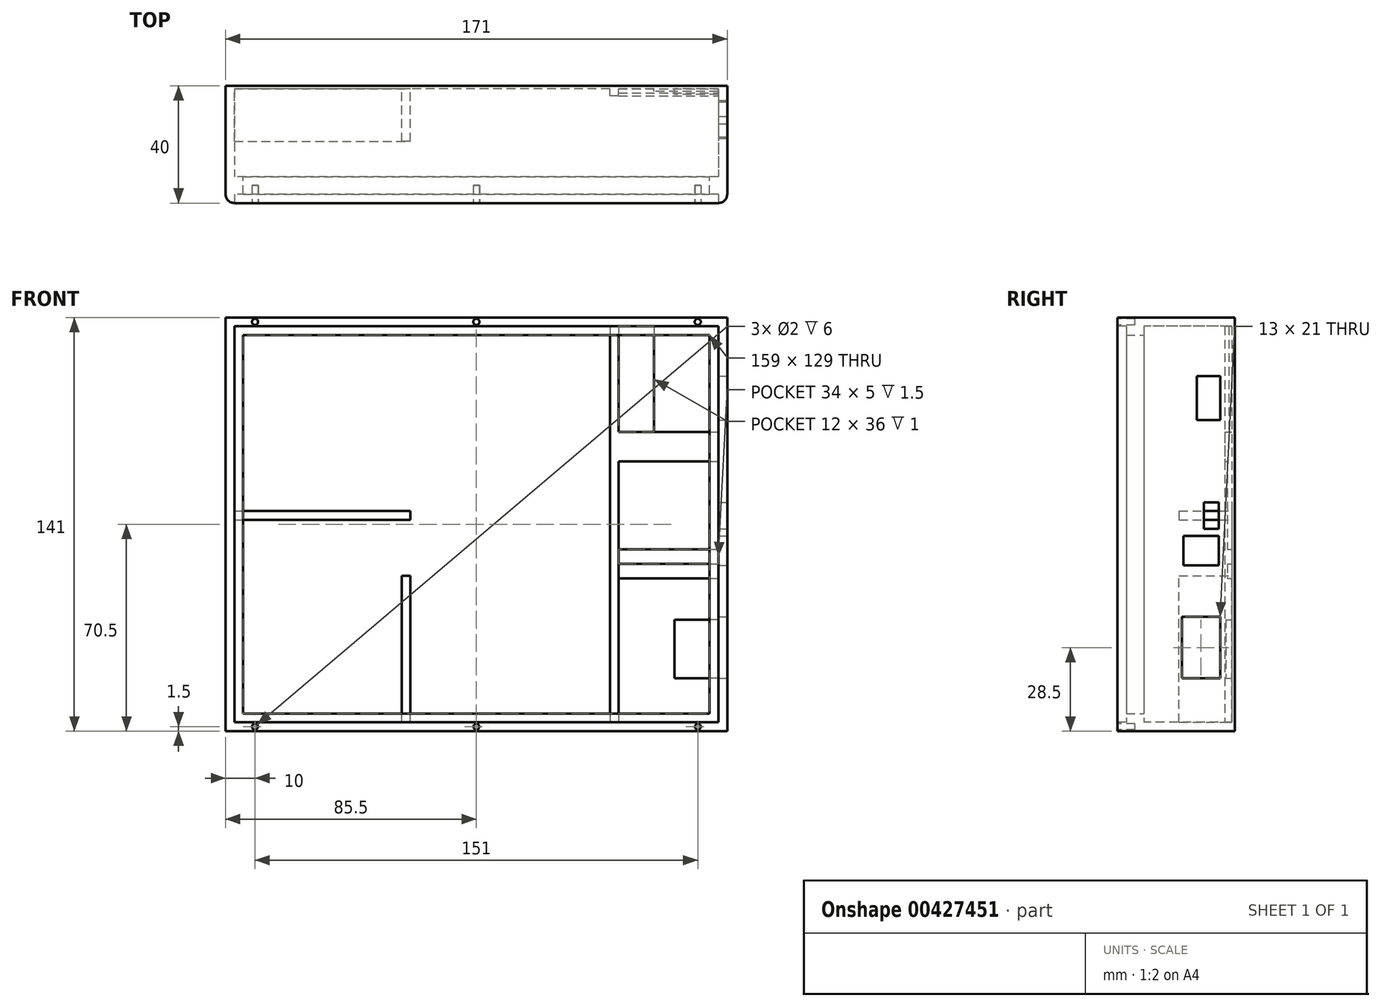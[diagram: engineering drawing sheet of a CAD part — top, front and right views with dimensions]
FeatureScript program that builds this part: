
annotation { "Feature Type Name" : "Feature", "Feature Type Description" : "" }
export const myFeature = defineFeature(function(context is Context, id is Id, definition is map)
    precondition{}
    {
        {
            var Q0;
            Q0=qCreatedBy(makeId("Front.planeOp"),FACE);
            var sketch = newSketch(context, id + "F0", { "sketchPlane" : qUnion([Q0])});
            skLineSegment(sketch, "E0.bottom", {"start": v(0, 0) * mm, "end": v(171, 0) * mm});
            skLineSegment(sketch, "E0.top", {"start": v(0, 141) * mm, "end": v(171, 141) * mm});
            skLineSegment(sketch, "E0.left", {"start": v(0, 0) * mm, "end": v(0, 141) * mm});
            skLineSegment(sketch, "E0.right", {"start": v(171, 0) * mm, "end": v(171, 141) * mm});
            skSolve(sketch);
        }
        {
            var Q0;
            Q0 = qSketchRegion(id + "F0", true);
            extrude(context, id + "F1", {"entities" : qUnion([Q0]), "depth" : 40 * mm});
        }
        {
            var Q0;
            Q0=makeQuery(id+"F1.opExtrude","CAP_FACE",FACE,{"disambiguationData":[OSD([sQuery(id+"F0.wireOp",EDGE,"E0.bottom"),sQuery(id+"F0.wireOp",EDGE,"E0.top"),sQuery(id+"F0.wireOp",EDGE,"E0.left"),sQuery(id+"F0.wireOp",EDGE,"E0.right")])],"isStart":false});
            var sketch = newSketch(context, id + "F2", { "sketchPlane" : qUnion([Q0])});
            skLineSegment(sketch, "E1", {"start": v(85.5, 141) * mm, "end": v(85.5, 0) * mm});
            skLineSegment(sketch, "E2", {"start": v(0, 70.5) * mm, "end": v(171, 70.5) * mm});
            skLineSegment(sketch, "E3.bottom", {"start": v(168, 138) * mm, "end": v(3, 138) * mm});
            skLineSegment(sketch, "E3.top", {"start": v(168, 3) * mm, "end": v(3, 3) * mm});
            skLineSegment(sketch, "E3.left", {"start": v(168, 138) * mm, "end": v(168, 3) * mm});
            skLineSegment(sketch, "E3.right", {"start": v(3, 138) * mm, "end": v(3, 3) * mm});
            skPoint(sketch, "E3.middle", {"position": v(85.5, 70.5) * mm});
            skSolve(sketch);
        }
        {
            var Q0;
            Q0 = qSketchRegion(id + "F2", true);
            extrude(context, id + "F3", {"entities" : qUnion([Q0]), "operationType" : NewBodyOperationType.REMOVE, "oppositeDirection" : true, "depth" : 3 * mm});
        }
        {
            var Q0;
            Q0=makeQuery(id+"F3.boolean.opBoolean","COPY",FACE,{"derivedFrom":makeQuery(id+"F3.opExtrude","CAP_FACE",FACE,{"disambiguationData":[OSD([sQuery(id+"F2.wireOp",EDGE,"E3.bottom"),sQuery(id+"F2.wireOp",EDGE,"E3.top"),sQuery(id+"F2.wireOp",EDGE,"E3.left"),sQuery(id+"F2.wireOp",EDGE,"E3.right")])],"isStart":false})});
            var sketch = newSketch(context, id + "F4", { "sketchPlane" : qUnion([Q0])});
            skLineSegment(sketch, "E4.bottom", {"start": v(3, 138) * mm, "end": v(168, 138) * mm});
            skLineSegment(sketch, "E4.top", {"start": v(3, 3) * mm, "end": v(168, 3) * mm});
            skLineSegment(sketch, "E4.left", {"start": v(3, 138) * mm, "end": v(3, 3) * mm});
            skLineSegment(sketch, "E4.right", {"start": v(168, 138) * mm, "end": v(168, 3) * mm});
            skLineSegment(sketch, "E5", {"start": v(85.5, 138) * mm, "end": v(85.5, 3) * mm});
            skLineSegment(sketch, "E6", {"start": v(3, 70.5) * mm, "end": v(168, 70.5) * mm});
            skLineSegment(sketch, "E7.bottom", {"start": v(166, 136) * mm, "end": v(5, 136) * mm});
            skLineSegment(sketch, "E7.top", {"start": v(166, 5) * mm, "end": v(5, 5) * mm});
            skLineSegment(sketch, "E7.left", {"start": v(166, 136) * mm, "end": v(166, 5) * mm});
            skLineSegment(sketch, "E7.right", {"start": v(5, 136) * mm, "end": v(5, 5) * mm});
            skPoint(sketch, "E7.middle", {"position": v(85.5, 70.5) * mm});
            skSolve(sketch);
        }
        {
            var Q0;
            {var subQ0=sQuery(id+"F4.wireOp",EDGE,"E7.bottom");var subQ1=sQuery(id+"F4.wireOp",EDGE,"E5");var subQ2=makeQuery(id+"F4.imprint","INTERSECT",VERTEX,{"derivedFrom":[subQ1,subQ0]});Q0=makeQuery(id+"F4.imprint","IMPRINT",FACE,{"disambiguationData":[TD([[makeQuery(id+"F4.imprint","IMPRINT",EDGE,{"disambiguationData":[TD([[subQ2,-1.0]])],"derivedFrom":subQ1}),-1.0]])]});}
            var Q1;
            {var subQ0=sQuery(id+"F4.wireOp",EDGE,"E7.bottom");var subQ1=sQuery(id+"F4.wireOp",EDGE,"E5");var subQ2=makeQuery(id+"F4.imprint","INTERSECT",VERTEX,{"derivedFrom":[subQ1,subQ0]});Q1=makeQuery(id+"F4.imprint","IMPRINT",FACE,{"disambiguationData":[TD([[makeQuery(id+"F4.imprint","IMPRINT",EDGE,{"disambiguationData":[TD([[subQ2,-1.0]])],"derivedFrom":subQ1}),1.0]])]});}
            var Q2;
            {var subQ0=sQuery(id+"F4.wireOp",EDGE,"E6");var subQ1=sQuery(id+"F4.wireOp",EDGE,"E5");var subQ2=makeQuery(id+"F4.imprint","INTERSECT",VERTEX,{"derivedFrom":[subQ1,subQ0]});Q2=makeQuery(id+"F4.imprint","IMPRINT",FACE,{"disambiguationData":[TD([[makeQuery(id+"F4.imprint","IMPRINT",EDGE,{"disambiguationData":[TD([[subQ2,-1.0]])],"derivedFrom":subQ1}),1.0]])]});}
            var Q3;
            {var subQ0=sQuery(id+"F4.wireOp",EDGE,"E6");var subQ1=sQuery(id+"F4.wireOp",EDGE,"E5");var subQ2=makeQuery(id+"F4.imprint","INTERSECT",VERTEX,{"derivedFrom":[subQ1,subQ0]});Q3=makeQuery(id+"F4.imprint","IMPRINT",FACE,{"disambiguationData":[TD([[makeQuery(id+"F4.imprint","IMPRINT",EDGE,{"disambiguationData":[TD([[subQ2,-1.0]])],"derivedFrom":subQ1}),-1.0]])]});}
            extrude(context, id + "F5", {"entities" : qUnion([Q0, Q1, Q2, Q3]), "operationType" : NewBodyOperationType.REMOVE, "oppositeDirection" : true, "depth" : 3 * mm});
        }
        {
            var Q0;
            Q0=makeQuery(id+"F3.boolean.opBoolean","COPY",FACE,{"derivedFrom":makeQuery(id+"F3.opExtrude","CAP_FACE",FACE,{"disambiguationData":[OSD([sQuery(id+"F2.wireOp",EDGE,"E3.bottom"),sQuery(id+"F2.wireOp",EDGE,"E3.top"),sQuery(id+"F2.wireOp",EDGE,"E3.left"),sQuery(id+"F2.wireOp",EDGE,"E3.right")])],"isStart":false})});
            var sketch = newSketch(context, id + "F6", { "sketchPlane" : qUnion([Q0])});
            skLineSegment(sketch, "E8", {"start": v(85.5, 138) * mm, "end": v(85.5, 3) * mm});
            skLineSegment(sketch, "E9", {"start": v(3, 70.5) * mm, "end": v(168, 70.5) * mm});
            skLineSegment(sketch, "E10.bottom", {"start": v(3, 138) * mm, "end": v(85.5, 138) * mm});
            skLineSegment(sketch, "E10.top", {"start": v(3, 70.5) * mm, "end": v(85.5, 70.5) * mm});
            skLineSegment(sketch, "E10.left", {"start": v(3, 138) * mm, "end": v(3, 70.5) * mm});
            skLineSegment(sketch, "E10.right", {"start": v(85.5, 138) * mm, "end": v(85.5, 70.5) * mm});
            skLineSegment(sketch, "E11.bottom", {"start": v(168, 138) * mm, "end": v(85.5, 138) * mm});
            skLineSegment(sketch, "E11.top", {"start": v(168, 70.5) * mm, "end": v(85.5, 70.5) * mm});
            skLineSegment(sketch, "E11.left", {"start": v(168, 138) * mm, "end": v(168, 70.5) * mm});
            skLineSegment(sketch, "E12.bottom", {"start": v(168, 3) * mm, "end": v(85.5, 3) * mm});
            skLineSegment(sketch, "E12.left", {"start": v(168, 3) * mm, "end": v(168, 70.5) * mm});
            skLineSegment(sketch, "E12.right", {"start": v(85.5, 3) * mm, "end": v(85.5, 70.5) * mm});
            skLineSegment(sketch, "E13.bottom", {"start": v(3, 3) * mm, "end": v(85.5, 3) * mm});
            skLineSegment(sketch, "E13.left", {"start": v(3, 3) * mm, "end": v(3, 70.5) * mm});
            skSolve(sketch);
        }
        {
            var Q0;
            Q0 = qSketchRegion(id + "F6", true);
            extrude(context, id + "F7", {"entities" : qUnion([Q0]), "operationType" : NewBodyOperationType.REMOVE, "oppositeDirection" : true, "depth" : 36 * mm});
        }
        {
            var Q0;
            Q0=makeQuery(id+"F7.boolean.opBoolean","COPY",FACE,{"derivedFrom":makeQuery(id+"F7.opExtrude","CAP_FACE",FACE,{"disambiguationData":[OSD([sQuery(id+"F6.wireOp",EDGE,"E10.bottom"),sQuery(id+"F6.wireOp",EDGE,"E10.left"),sQuery(id+"F6.wireOp",EDGE,"E11.bottom"),sQuery(id+"F6.wireOp",EDGE,"E11.left"),sQuery(id+"F6.wireOp",EDGE,"E12.bottom"),sQuery(id+"F6.wireOp",EDGE,"E12.left"),sQuery(id+"F6.wireOp",EDGE,"E13.bottom"),sQuery(id+"F6.wireOp",EDGE,"E13.left")])],"isStart":false})});
            var sketch = newSketch(context, id + "F8", { "sketchPlane" : qUnion([Q0])});
            skLineSegment(sketch, "E14.bottom", {"start": v(3, 3) * mm, "end": v(168, 3) * mm});
            skLineSegment(sketch, "E14.top", {"start": v(3, 138) * mm, "end": v(168, 138) * mm});
            skLineSegment(sketch, "E14.left", {"start": v(3, 3) * mm, "end": v(3, 138) * mm});
            skLineSegment(sketch, "E14.right", {"start": v(168, 3) * mm, "end": v(168, 138) * mm});
            skLineSegment(sketch, "E15", {"start": v(85.5, 3) * mm, "end": v(85.5, 138) * mm});
            skLineSegment(sketch, "E16", {"start": v(3, 70.5) * mm, "end": v(168, 70.5) * mm});
            skLineSegment(sketch, "E17.bottom", {"start": v(6, 135) * mm, "end": v(165, 135) * mm});
            skLineSegment(sketch, "E17.top", {"start": v(6, 6) * mm, "end": v(165, 6) * mm});
            skLineSegment(sketch, "E17.left", {"start": v(6, 135) * mm, "end": v(6, 6) * mm});
            skLineSegment(sketch, "E17.right", {"start": v(165, 135) * mm, "end": v(165, 6) * mm});
            skPoint(sketch, "E17.middle", {"position": v(85.5, 70.5) * mm});
            skSolve(sketch);
        }
        {
            var Q0;
            {var subQ1=sQuery(id+"F8.wireOp",EDGE,"E14.left");var subQ6=sQuery(id+"F8.wireOp",EDGE,"E14.top");var subQ10=makeQuery(id+"F8.imprint","INTERSECT",VERTEX,{"derivedFrom":[subQ6,subQ1]});Q0=makeQuery(id+"F8.imprint","IMPRINT",FACE,{"disambiguationData":[TD([[makeQuery(id+"F8.imprint","IMPRINT",EDGE,{"disambiguationData":[TD([[subQ10,1.0]])],"derivedFrom":subQ6}),1.0]])]});}
            var Q1;
            {var subQ1=sQuery(id+"F8.wireOp",EDGE,"E14.left");var subQ5=sQuery(id+"F8.wireOp",EDGE,"E14.bottom");var subQ6=makeQuery(id+"F8.imprint","INTERSECT",VERTEX,{"derivedFrom":[subQ5,subQ1]});Q1=makeQuery(id+"F8.imprint","IMPRINT",FACE,{"disambiguationData":[TD([[makeQuery(id+"F8.imprint","IMPRINT",EDGE,{"disambiguationData":[TD([[subQ6,1.0]])],"derivedFrom":subQ5}),-1.0]])]});}
            var Q2;
            {var subQ1=sQuery(id+"F8.wireOp",EDGE,"E14.bottom");var subQ7=sQuery(id+"F8.wireOp",EDGE,"E14.right");var subQ8=makeQuery(id+"F8.imprint","INTERSECT",VERTEX,{"derivedFrom":[subQ1,subQ7]});Q2=makeQuery(id+"F8.imprint","IMPRINT",FACE,{"disambiguationData":[TD([[makeQuery(id+"F8.imprint","IMPRINT",EDGE,{"disambiguationData":[TD([[subQ8,-1.0]])],"derivedFrom":subQ1}),-1.0]])]});}
            var Q3;
            {var subQ1=sQuery(id+"F8.wireOp",EDGE,"E14.right");var subQ6=sQuery(id+"F8.wireOp",EDGE,"E14.top");var subQ11=makeQuery(id+"F8.imprint","INTERSECT",VERTEX,{"derivedFrom":[subQ6,subQ1]});Q3=makeQuery(id+"F8.imprint","IMPRINT",FACE,{"disambiguationData":[TD([[makeQuery(id+"F8.imprint","IMPRINT",EDGE,{"disambiguationData":[TD([[subQ11,-1.0]])],"derivedFrom":subQ6}),1.0]])]});}
            extrude(context, id + "F9", {"entities" : qUnion([Q0, Q1, Q2, Q3]), "operationType" : NewBodyOperationType.ADD, "depth" : 36 * mm, "hasSecondDirection" : true, "secondDirectionOppositeDirection" : false, "secondDirectionDepth" : 30 * mm});
        }
        {
            var Q0;
            Q0=makeQuery(id+"F1.opExtrude","SWEPT_FACE",FACE,{"disambiguationData":[OSD([sQuery(id+"F0.wireOp",EDGE,"E0.right")])]});
            var sketch = newSketch(context, id + "F10", { "sketchPlane" : qUnion([Q0])});
            skLineSegment(sketch, "E18.bottom", {"start": v(-13, 106) * mm, "end": v(-5, 106) * mm});
            skLineSegment(sketch, "E18.top", {"start": v(-13, 121) * mm, "end": v(-5, 121) * mm});
            skLineSegment(sketch, "E18.left", {"start": v(-13, 106) * mm, "end": v(-13, 121) * mm});
            skLineSegment(sketch, "E18.right", {"start": v(-5, 106) * mm, "end": v(-5, 121) * mm});
            skLineSegment(sketch, "E19", {"start": v(-9, 121) * mm, "end": v(-9, 141) * mm});
            skLineSegment(sketch, "E20", {"start": v(-5, 113.5) * mm, "end": v(0, 113.5) * mm});
            skSolve(sketch);
        }
        {
            var Q0;
            {var subQ5=sQuery(id+"F10.wireOp",EDGE,"E18.bottom");Q0=makeQuery(id+"F10.imprint","IMPRINT",FACE,{"disambiguationData":[TD([[makeQuery(id+"F10.imprint","IMPRINT",EDGE,{"derivedFrom":subQ5}),1.0]])]});}
            extrude(context, id + "F11", {"entities" : qUnion([Q0]), "operationType" : NewBodyOperationType.REMOVE, "oppositeDirection" : true, "depth" : 39.9 * mm});
        }
        {
            var Q0;
            Q0=makeQuery(id+"F1.opExtrude","CAP_EDGE",EDGE,{"disambiguationData":[OSD([sQuery(id+"F0.wireOp",EDGE,"E0.right")])],"isStart":false});
            fillet(context, id + "F12", {"entities" : qUnion([Q0]), "radius" : 3 * mm, "tangentPropagation" : true, "allowEdgeOverflow" : false});
        }
        {
            var Q0;
            Q0=makeQuery(id+"F1.opExtrude","CAP_EDGE",EDGE,{"disambiguationData":[OSD([sQuery(id+"F0.wireOp",EDGE,"E0.left")])],"isStart":false});
            fillet(context, id + "F13", {"entities" : qUnion([Q0]), "radius" : 3 * mm, "tangentPropagation" : true, "allowEdgeOverflow" : false});
        }
        {
            var Q0;
            Q0=makeQuery(id+"F1.opExtrude","SWEPT_FACE",FACE,{"disambiguationData":[OSD([sQuery(id+"F0.wireOp",EDGE,"E0.right")])]});
            var sketch = newSketch(context, id + "F14", { "sketchPlane" : qUnion([Q0])});
            skLineSegment(sketch, "E21.bottom", {"start": v(-10.5, 69) * mm, "end": v(-5.5, 69) * mm});
            skLineSegment(sketch, "E21.top", {"start": v(-10.5, 78) * mm, "end": v(-5.5, 78) * mm});
            skLineSegment(sketch, "E21.left", {"start": v(-10.5, 69) * mm, "end": v(-10.5, 78) * mm});
            skLineSegment(sketch, "E21.right", {"start": v(-5.5, 69) * mm, "end": v(-5.5, 78) * mm});
            skLineSegment(sketch, "E22", {"start": v(-8, 78) * mm, "end": v(-8, 138) * mm});
            skLineSegment(sketch, "E23", {"start": v(-5.5, 73.5) * mm, "end": v(0, 73.5) * mm});
            skSolve(sketch);
        }
        {
            var Q0;
            {var subQ5=sQuery(id+"F14.wireOp",EDGE,"E21.bottom");Q0=makeQuery(id+"F14.imprint","IMPRINT",FACE,{"disambiguationData":[TD([[makeQuery(id+"F14.imprint","IMPRINT",EDGE,{"derivedFrom":subQ5}),1.0]])]});}
            extrude(context, id + "F15", {"entities" : qUnion([Q0]), "operationType" : NewBodyOperationType.REMOVE, "oppositeDirection" : true, "depth" : 87.6 * mm});
        }
        {
            var Q0;
            Q0=makeQuery(id+"F1.opExtrude","SWEPT_FACE",FACE,{"disambiguationData":[OSD([sQuery(id+"F0.wireOp",EDGE,"E0.right")])]});
            var sketch = newSketch(context, id + "F16", { "sketchPlane" : qUnion([Q0])});
            skLineSegment(sketch, "E24.bottom", {"start": v(-17.5, 56.5) * mm, "end": v(-5.5, 56.5) * mm});
            skLineSegment(sketch, "E24.top", {"start": v(-17.5, 66.5) * mm, "end": v(-5.5, 66.5) * mm});
            skLineSegment(sketch, "E24.left", {"start": v(-17.5, 56.5) * mm, "end": v(-17.5, 66.5) * mm});
            skLineSegment(sketch, "E24.right", {"start": v(-5.5, 56.5) * mm, "end": v(-5.5, 66.5) * mm});
            skLineSegment(sketch, "E25", {"start": v(-11.5, 66.5) * mm, "end": v(-11.5, 138) * mm});
            skLineSegment(sketch, "E26", {"start": v(-5.5, 61.5) * mm, "end": v(0, 61.5) * mm});
            skSolve(sketch);
        }
        {
            var Q0;
            {var subQ5=sQuery(id+"F16.wireOp",EDGE,"E24.bottom");Q0=makeQuery(id+"F16.imprint","IMPRINT",FACE,{"disambiguationData":[TD([[makeQuery(id+"F16.imprint","IMPRINT",EDGE,{"derivedFrom":subQ5}),1.0]])]});}
            extrude(context, id + "F17", {"entities" : qUnion([Q0]), "operationType" : NewBodyOperationType.REMOVE, "oppositeDirection" : true, "depth" : 58 * mm});
        }
        {
            var Q0;
            Q0=makeQuery(id+"F7.boolean.opBoolean","COPY",FACE,{"derivedFrom":makeQuery(id+"F7.opExtrude","CAP_FACE",FACE,{"disambiguationData":[OSD([sQuery(id+"F6.wireOp",EDGE,"E10.bottom"),sQuery(id+"F6.wireOp",EDGE,"E10.left"),sQuery(id+"F6.wireOp",EDGE,"E11.bottom"),sQuery(id+"F6.wireOp",EDGE,"E11.left"),sQuery(id+"F6.wireOp",EDGE,"E12.bottom"),sQuery(id+"F6.wireOp",EDGE,"E12.left"),sQuery(id+"F6.wireOp",EDGE,"E13.bottom"),sQuery(id+"F6.wireOp",EDGE,"E13.left")])],"isStart":false})});
            var sketch = newSketch(context, id + "F18", { "sketchPlane" : qUnion([Q0])});
            skLineSegment(sketch, "E27.bottom", {"start": v(131, 138) * mm, "end": v(134, 138) * mm});
            skLineSegment(sketch, "E27.top", {"start": v(131, 3) * mm, "end": v(134, 3) * mm});
            skLineSegment(sketch, "E27.left", {"start": v(131, 138) * mm, "end": v(131, 3) * mm});
            skLineSegment(sketch, "E27.right", {"start": v(134, 138) * mm, "end": v(134, 3) * mm});
            skLineSegment(sketch, "E28", {"start": v(134, 70.5) * mm, "end": v(168, 70.5) * mm});
            skLineSegment(sketch, "E29.bottom", {"start": v(134, 102) * mm, "end": v(168, 102) * mm});
            skLineSegment(sketch, "E29.top", {"start": v(134, 92) * mm, "end": v(168, 92) * mm});
            skLineSegment(sketch, "E29.left", {"start": v(134, 102) * mm, "end": v(134, 92) * mm});
            skLineSegment(sketch, "E29.right", {"start": v(168, 102) * mm, "end": v(168, 92) * mm});
            skLineSegment(sketch, "E30", {"start": v(151, 102) * mm, "end": v(151, 138) * mm});
            skSolve(sketch);
        }
        {
            var Q0;
            {var subQ1=sQuery(id+"F18.wireOp",EDGE,"E27.bottom");Q0=makeQuery(id+"F18.imprint","IMPRINT",FACE,{"disambiguationData":[TD([[makeQuery(id+"F18.imprint","IMPRINT",EDGE,{"derivedFrom":subQ1}),1.0]])]});}
            var Q1;
            Q1=makeQuery(id+"F18.imprint","IMPRINT",FACE,{"disambiguationData":[TD([[makeQuery(id+"F18.imprint","IMPRINT",EDGE,{"derivedFrom":sQuery(id+"F18.wireOp",EDGE,"E29.top")}),1.0]])]});
            extrude(context, id + "F19", {"entities" : qUnion([Q0, Q1]), "operationType" : NewBodyOperationType.ADD, "depth" : 2.5 * mm});
        }
        {
            var Q0;
            {var subQ0=sQuery(id+"F6.wireOp",EDGE,"E12.left");var subQ1=sQuery(id+"F6.wireOp",EDGE,"E11.left");var subQ2=sQuery(id+"F6.wireOp",EDGE,"E13.bottom");var subQ3=sQuery(id+"F6.wireOp",EDGE,"E12.bottom");var subQ4=sQuery(id+"F18.wireOp",EDGE,"E29.top");Q0=makeQuery(id+"F19.boolean.opBoolean","SPLIT",FACE,{"disambiguationData":[TD([makeQuery(id+"F19.opExtrude","SWEPT_FACE",FACE,{"disambiguationData":[OSD([subQ4])]})])],"derivedFrom":makeQuery(id+"F7.boolean.opBoolean","COPY",FACE,{"derivedFrom":makeQuery(id+"F7.opExtrude","CAP_FACE",FACE,{"disambiguationData":[OSD([sQuery(id+"F6.wireOp",EDGE,"E10.bottom"),sQuery(id+"F6.wireOp",EDGE,"E10.left"),sQuery(id+"F6.wireOp",EDGE,"E11.bottom"),subQ1,subQ3,subQ0,subQ2,sQuery(id+"F6.wireOp",EDGE,"E13.left")])],"isStart":false})})});}
            var sketch = newSketch(context, id + "F20", { "sketchPlane" : qUnion([Q0])});
            skLineSegment(sketch, "E31.bottom", {"start": v(134, 92) * mm, "end": v(168, 92) * mm});
            skLineSegment(sketch, "E31.top", {"start": v(134, 62) * mm, "end": v(168, 62) * mm});
            skLineSegment(sketch, "E31.left", {"start": v(134, 92) * mm, "end": v(134, 62) * mm});
            skLineSegment(sketch, "E31.right", {"start": v(168, 92) * mm, "end": v(168, 62) * mm});
            skLineSegment(sketch, "E32.bottom", {"start": v(134, 57) * mm, "end": v(168, 57) * mm});
            skLineSegment(sketch, "E32.top", {"start": v(134, 52) * mm, "end": v(168, 52) * mm});
            skLineSegment(sketch, "E32.left", {"start": v(134, 57) * mm, "end": v(134, 52) * mm});
            skLineSegment(sketch, "E32.right", {"start": v(168, 57) * mm, "end": v(168, 52) * mm});
            skLineSegment(sketch, "E33", {"start": v(134, 62) * mm, "end": v(134, 57) * mm});
            skSolve(sketch);
        }
        {
            var Q0;
            Q0=makeQuery(id+"F20.imprint","IMPRINT",FACE,{"disambiguationData":[TD([[makeQuery(id+"F20.imprint","IMPRINT",EDGE,{"derivedFrom":sQuery(id+"F20.wireOp",EDGE,"E31.bottom")}),-1.0]])]});
            var Q1;
            Q1=makeQuery(id+"F20.imprint","IMPRINT",FACE,{"disambiguationData":[TD([[makeQuery(id+"F20.imprint","IMPRINT",EDGE,{"derivedFrom":sQuery(id+"F20.wireOp",EDGE,"E32.bottom")}),-1.0]])]});
            extrude(context, id + "F21", {"entities" : qUnion([Q0, Q1]), "operationType" : NewBodyOperationType.ADD, "depth" : 1.5 * mm});
        }
        {
            var Q0;
            {var subQ0=sQuery(id+"F6.wireOp",EDGE,"E12.left");var subQ1=sQuery(id+"F6.wireOp",EDGE,"E11.left");var subQ2=sQuery(id+"F18.wireOp",EDGE,"E29.bottom");var subQ3=sQuery(id+"F6.wireOp",EDGE,"E11.bottom");var subQ4=sQuery(id+"F6.wireOp",EDGE,"E10.bottom");Q0=makeQuery(id+"F19.boolean.opBoolean","SPLIT",FACE,{"disambiguationData":[TD([makeQuery(id+"F19.opExtrude","SWEPT_FACE",FACE,{"disambiguationData":[OSD([subQ2])]})])],"derivedFrom":makeQuery(id+"F7.boolean.opBoolean","COPY",FACE,{"derivedFrom":makeQuery(id+"F7.opExtrude","CAP_FACE",FACE,{"disambiguationData":[OSD([subQ4,sQuery(id+"F6.wireOp",EDGE,"E10.left"),subQ3,subQ1,sQuery(id+"F6.wireOp",EDGE,"E12.bottom"),subQ0,sQuery(id+"F6.wireOp",EDGE,"E13.bottom"),sQuery(id+"F6.wireOp",EDGE,"E13.left")])],"isStart":false})})});}
            var sketch = newSketch(context, id + "F22", { "sketchPlane" : qUnion([Q0])});
            skLineSegment(sketch, "E34.bottom", {"start": v(146, 138) * mm, "end": v(168, 138) * mm});
            skLineSegment(sketch, "E34.top", {"start": v(146, 102) * mm, "end": v(168, 102) * mm});
            skLineSegment(sketch, "E34.left", {"start": v(146, 138) * mm, "end": v(146, 102) * mm});
            skLineSegment(sketch, "E34.right", {"start": v(168, 138) * mm, "end": v(168, 102) * mm});
            skSolve(sketch);
        }
        {
            var Q0;
            Q0 = qSketchRegion(id + "F22", true);
            extrude(context, id + "F23", {"entities" : qUnion([Q0]), "operationType" : NewBodyOperationType.ADD, "depth" : 1 * mm});
        }
        {
            var Q0;
            Q0=makeQuery(id+"F1.opExtrude","SWEPT_FACE",FACE,{"disambiguationData":[OSD([sQuery(id+"F0.wireOp",EDGE,"E0.right")])]});
            var sketch = newSketch(context, id + "F24", { "sketchPlane" : qUnion([Q0])});
            skLineSegment(sketch, "E35.bottom", {"start": v(-18, 18) * mm, "end": v(-5, 18) * mm});
            skLineSegment(sketch, "E35.top", {"start": v(-18, 39) * mm, "end": v(-5, 39) * mm});
            skLineSegment(sketch, "E35.left", {"start": v(-18, 18) * mm, "end": v(-18, 39) * mm});
            skLineSegment(sketch, "E35.right", {"start": v(-5, 18) * mm, "end": v(-5, 39) * mm});
            skLineSegment(sketch, "E36", {"start": v(-11.5, 18) * mm, "end": v(-11.5, 3) * mm});
            skLineSegment(sketch, "E37", {"start": v(-5, 28.5) * mm, "end": v(0, 28.5) * mm});
            skSolve(sketch);
        }
        {
            var Q0;
            Q0 = qSketchRegion(id + "F24", true);
            extrude(context, id + "F25", {"entities" : qUnion([Q0]), "operationType" : NewBodyOperationType.REMOVE, "oppositeDirection" : true, "depth" : 107.7 * mm});
        }
        {
            var Q0;
            {var subQ0=sQuery(id+"F6.wireOp",EDGE,"E12.left");var subQ1=sQuery(id+"F6.wireOp",EDGE,"E11.left");var subQ4=sQuery(id+"F6.wireOp",EDGE,"E13.bottom");var subQ5=sQuery(id+"F6.wireOp",EDGE,"E12.bottom");var subQ7=makeQuery(id+"F3.boolean.opBoolean","COPY",FACE,{"derivedFrom":makeQuery(id+"F3.opExtrude","SWEPT_FACE",FACE,{"disambiguationData":[OSD([sQuery(id+"F2.wireOp",EDGE,"E3.top")])]})});var subQ10=sQuery(id+"F18.wireOp",EDGE,"E29.top");Q0=makeQuery(id+"F21.boolean.opBoolean","SPLIT",FACE,{"disambiguationData":[TD([subQ7])],"derivedFrom":makeQuery(id+"F19.boolean.opBoolean","SPLIT",FACE,{"disambiguationData":[TD([makeQuery(id+"F19.opExtrude","SWEPT_FACE",FACE,{"disambiguationData":[OSD([subQ10])]})])],"derivedFrom":makeQuery(id+"F7.boolean.opBoolean","COPY",FACE,{"derivedFrom":makeQuery(id+"F7.opExtrude","CAP_FACE",FACE,{"disambiguationData":[OSD([sQuery(id+"F6.wireOp",EDGE,"E10.bottom"),sQuery(id+"F6.wireOp",EDGE,"E10.left"),sQuery(id+"F6.wireOp",EDGE,"E11.bottom"),subQ1,subQ5,subQ0,subQ4,sQuery(id+"F6.wireOp",EDGE,"E13.left")])],"isStart":false})})})});}
            var sketch = newSketch(context, id + "F26", { "sketchPlane" : qUnion([Q0])});
            skLineSegment(sketch, "E38.bottom", {"start": v(168, 38) * mm, "end": v(153, 38) * mm});
            skLineSegment(sketch, "E38.top", {"start": v(168, 18) * mm, "end": v(153, 18) * mm});
            skLineSegment(sketch, "E38.left", {"start": v(168, 38) * mm, "end": v(168, 18) * mm});
            skLineSegment(sketch, "E38.right", {"start": v(153, 38) * mm, "end": v(153, 18) * mm});
            skLineSegment(sketch, "E39", {"start": v(160.5, 18) * mm, "end": v(160.5, 3) * mm});
            skSolve(sketch);
        }
        {
            var Q0;
            Q0 = qSketchRegion(id + "F26", true);
            extrude(context, id + "F27", {"entities" : qUnion([Q0]), "operationType" : NewBodyOperationType.ADD, "depth" : 2 * mm});
        }
        {
            var Q0;
            {var subQ0=sQuery(id+"F6.wireOp",EDGE,"E11.bottom");var subQ1=sQuery(id+"F6.wireOp",EDGE,"E10.bottom");var subQ2=sQuery(id+"F6.wireOp",EDGE,"E13.bottom");var subQ3=sQuery(id+"F6.wireOp",EDGE,"E12.bottom");var subQ4=sQuery(id+"F6.wireOp",EDGE,"E13.left");var subQ5=sQuery(id+"F6.wireOp",EDGE,"E10.left");Q0=makeQuery(id+"F19.boolean.opBoolean","SPLIT",FACE,{"disambiguationData":[TD([makeQuery(id+"F3.boolean.opBoolean","COPY",FACE,{"derivedFrom":makeQuery(id+"F3.opExtrude","SWEPT_FACE",FACE,{"disambiguationData":[OSD([sQuery(id+"F2.wireOp",EDGE,"E3.right")])]})})])],"derivedFrom":makeQuery(id+"F7.boolean.opBoolean","COPY",FACE,{"derivedFrom":makeQuery(id+"F7.opExtrude","CAP_FACE",FACE,{"disambiguationData":[OSD([subQ1,subQ5,subQ0,sQuery(id+"F6.wireOp",EDGE,"E11.left"),subQ3,sQuery(id+"F6.wireOp",EDGE,"E12.left"),subQ2,subQ4])],"isStart":false})})});}
            var sketch = newSketch(context, id + "F28", { "sketchPlane" : qUnion([Q0])});
            skLineSegment(sketch, "E40.bottom", {"start": v(3, 75) * mm, "end": v(63, 75) * mm});
            skLineSegment(sketch, "E40.top", {"start": v(3, 72) * mm, "end": v(63, 72) * mm});
            skLineSegment(sketch, "E40.left", {"start": v(3, 75) * mm, "end": v(3, 72) * mm});
            skLineSegment(sketch, "E40.right", {"start": v(63, 75) * mm, "end": v(63, 72) * mm});
            skLineSegment(sketch, "E41", {"start": v(33, 72) * mm, "end": v(33, 3) * mm});
            skLineSegment(sketch, "E42.bottom", {"start": v(63, 3) * mm, "end": v(60, 3) * mm});
            skLineSegment(sketch, "E42.top", {"start": v(63, 53) * mm, "end": v(60, 53) * mm});
            skLineSegment(sketch, "E42.left", {"start": v(63, 3) * mm, "end": v(63, 53) * mm});
            skLineSegment(sketch, "E42.right", {"start": v(60, 3) * mm, "end": v(60, 53) * mm});
            skLineSegment(sketch, "E43", {"start": v(60, 28) * mm, "end": v(3, 28) * mm});
            skSolve(sketch);
        }
        {
            var Q0;
            Q0 = qSketchRegion(id + "F28", true);
            extrude(context, id + "F29", {"entities" : qUnion([Q0]), "operationType" : NewBodyOperationType.ADD, "depth" : 18 * mm});
        }
        {
            var Q0;
            Q0=makeQuery(id+"F13.opFillet","SPLIT",FACE,{"disambiguationData":[OD(0.0)],"derivedFrom":makeQuery(id+"F1.opExtrude","CAP_FACE",FACE,{"disambiguationData":[OSD([sQuery(id+"F0.wireOp",EDGE,"E0.bottom"),sQuery(id+"F0.wireOp",EDGE,"E0.top"),sQuery(id+"F0.wireOp",EDGE,"E0.left"),sQuery(id+"F0.wireOp",EDGE,"E0.right")])],"isStart":false})});
            var sketch = newSketch(context, id + "F30", { "sketchPlane" : qUnion([Q0])});
            skCircle(sketch, "E44", {"center": v(10.05, 139.5) * mm, "radius": 1.05 * mm});
            skLineSegment(sketch, "E45", {"start": v(10.05, 139.5) * mm, "end": v(10.05, 141) * mm});
            skLineSegment(sketch, "E46", {"start": v(3, 139.5) * mm, "end": v(9, 139.5) * mm});
            skCircle(sketch, "E47", {"center": v(160.95, 139.5) * mm, "radius": 1.05 * mm});
            skLineSegment(sketch, "E48", {"start": v(160.95, 139.5) * mm, "end": v(160.95, 141) * mm});
            skLineSegment(sketch, "E49", {"start": v(168, 139.5) * mm, "end": v(162, 139.5) * mm});
            skLineSegment(sketch, "E50", {"start": v(3, 139.5) * mm, "end": v(168, 139.5) * mm});
            skCircle(sketch, "E51", {"center": v(85.5, 139.5) * mm, "radius": 1.05 * mm});
            skSolve(sketch);
        }
        {
            var Q0;
            Q0 = qSketchRegion(id + "F30", true);
            extrude(context, id + "F31", {"entities" : qUnion([Q0]), "operationType" : NewBodyOperationType.REMOVE, "oppositeDirection" : true, "depth" : 6 * mm});
        }
        {
            var Q0;
            Q0=makeQuery(id+"F13.opFillet","SPLIT",FACE,{"disambiguationData":[OD(1.0)],"derivedFrom":makeQuery(id+"F1.opExtrude","CAP_FACE",FACE,{"disambiguationData":[OSD([sQuery(id+"F0.wireOp",EDGE,"E0.bottom"),sQuery(id+"F0.wireOp",EDGE,"E0.top"),sQuery(id+"F0.wireOp",EDGE,"E0.left"),sQuery(id+"F0.wireOp",EDGE,"E0.right")])],"isStart":false})});
            var sketch = newSketch(context, id + "F32", { "sketchPlane" : qUnion([Q0])});
            skCircle(sketch, "E52", {"center": v(10, 1.5) * mm, "radius": 1 * mm});
            skLineSegment(sketch, "E53", {"start": v(10, 1.5) * mm, "end": v(10, 3) * mm});
            skLineSegment(sketch, "E54", {"start": v(3, 1.5) * mm, "end": v(9, 1.5) * mm});
            skCircle(sketch, "E55", {"center": v(161, 1.5) * mm, "radius": 1 * mm});
            skLineSegment(sketch, "E56", {"start": v(161, 1.5) * mm, "end": v(161, 3) * mm});
            skLineSegment(sketch, "E57", {"start": v(168, 1.5) * mm, "end": v(162, 1.5) * mm});
            skLineSegment(sketch, "E58", {"start": v(3, 1.5) * mm, "end": v(168, 1.5) * mm});
            skCircle(sketch, "E59", {"center": v(85.5, 1.5) * mm, "radius": 1 * mm});
            skSolve(sketch);
        }
        {
            var Q0;
            Q0 = qSketchRegion(id + "F32", true);
            extrude(context, id + "F33", {"entities" : qUnion([Q0]), "operationType" : NewBodyOperationType.REMOVE, "oppositeDirection" : true, "depth" : 6 * mm});
        }
    });
